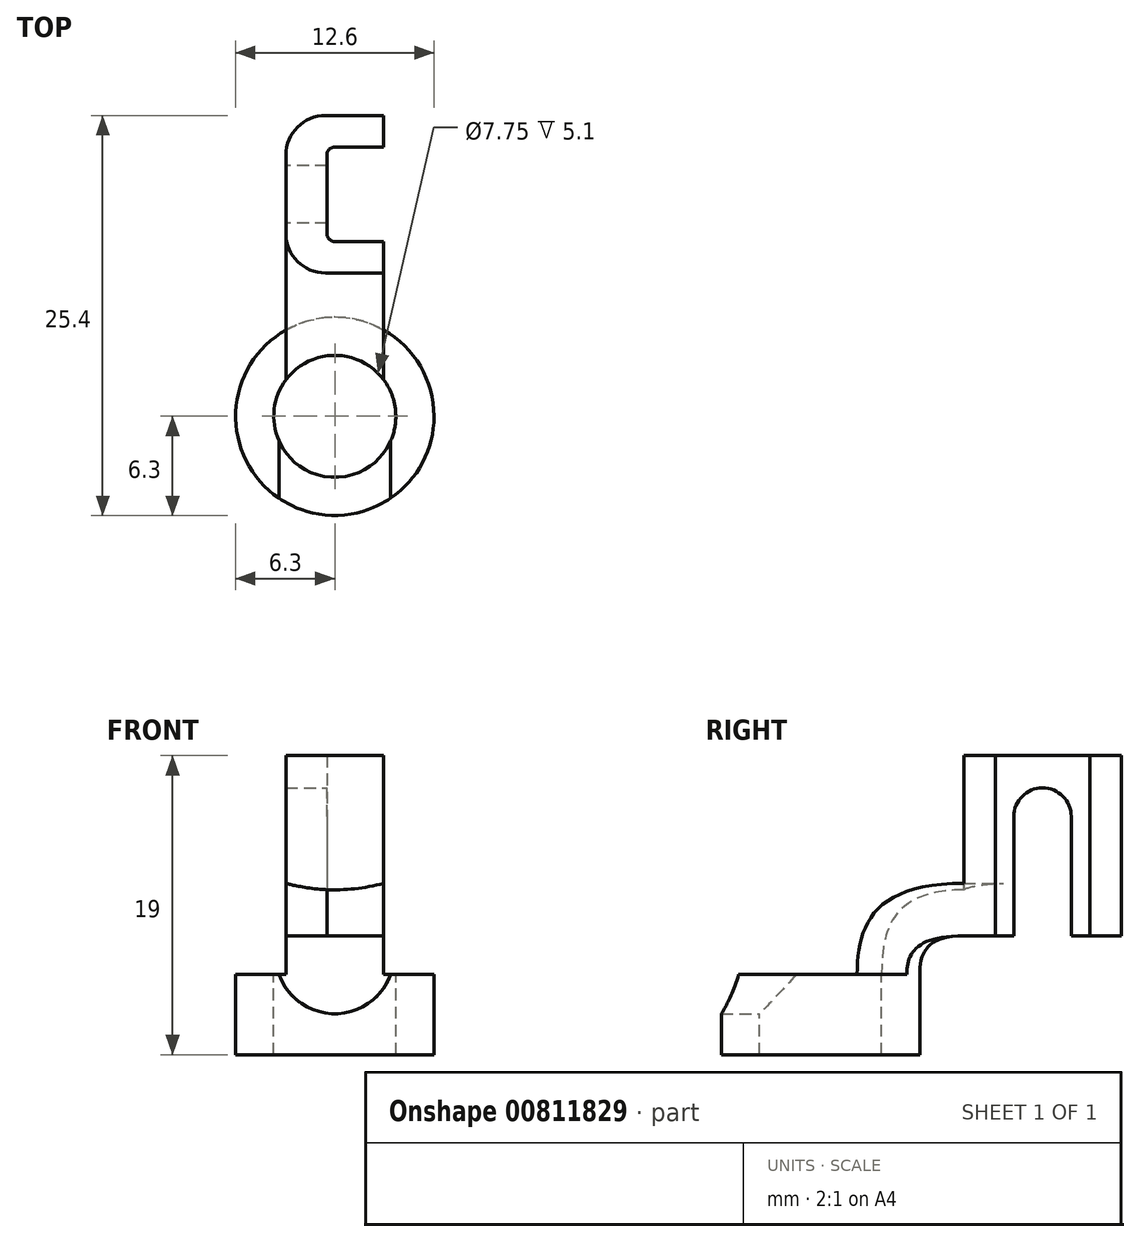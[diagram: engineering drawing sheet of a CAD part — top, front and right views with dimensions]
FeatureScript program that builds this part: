
annotation { "Feature Type Name" : "Feature", "Feature Type Description" : "" }
export const myFeature = defineFeature(function(context is Context, id is Id, definition is map)
    precondition{}
    {
        {
            var Q0;
            Q0=qCreatedBy(makeId("Top.planeOp"),FACE);
            var sketch = newSketch(context, id + "F0", { "sketchPlane" : qUnion([Q0])});
            skCircle(sketch, "E0", {"center": v(0, 0) * mm, "radius": 3.88 * mm});
            skCircle(sketch, "E1", {"center": v(0, 0) * mm, "radius": 6.3 * mm});
            skSolve(sketch);
        }
        {
            var Q0;
            Q0=qSketchRegion(id+"F0",true);
            extrude(context, id + "F1", {"entities" : qUnion([Q0]), "oppositeDirection" : true, "depth" : 5.1 * mm, "offsetDistance" : 25 * mm});
        }
        {
            var Q0;
            Q0=makeQuery(id+"F1.opExtrude","CAP_FACE",FACE,{"disambiguationData":[OSD([sQuery(id+"F0.wireOp",EDGE,"E0"),sQuery(id+"F0.wireOp",EDGE,"E1")])],"isStart":true});
            cPlane(context, id + "F2", {"entities" : qUnion([Q0]), "cplaneType" : CPlaneType.OFFSET, "offset" : (7.55 - 5.1) * mm, "width" : 150 * mm, "height" : 150 * mm});
        }
        {
            var Q0;
            Q0=qCreatedBy(id+"F2.planeOp",FACE);
            var sketch = newSketch(context, id + "F3", { "sketchPlane" : qUnion([Q0])});
            skLineSegment(sketch, "E2.bottom", {"start": v(-3.1, 9.1) * mm, "end": v(3.1, 9.1) * mm});
            skLineSegment(sketch, "E2.top", {"start": v(-3.1, 19.1) * mm, "end": v(3.1, 19.1) * mm});
            skLineSegment(sketch, "E2.left", {"start": v(-3.1, 9.1) * mm, "end": v(-3.1, 19.1) * mm});
            skLineSegment(sketch, "E2.right", {"start": v(3.1, 9.1) * mm, "end": v(3.1, 11.1) * mm});
            skLineSegment(sketch, "E3", {"start": v(-3.1, 14.1) * mm, "end": v(3.1, 14.1) * mm, "construction": true});
            skLineSegment(sketch, "E4", {"start": v(3.1, 17.1) * mm, "end": v(-0.5, 17.1) * mm});
            skLineSegment(sketch, "E5", {"start": v(-0.5, 17.1) * mm, "end": v(-0.5, 14.1) * mm});
            skLineSegment(sketch, "E6.MirrorCS", {"start": v(3.1, 11.1) * mm, "end": v(-0.5, 11.1) * mm});
            skLineSegment(sketch, "E7.MirrorCS", {"start": v(-0.5, 11.1) * mm, "end": v(-0.5, 14.1) * mm});
            skLineSegment(sketch, "E8.trimOffspring", {"start": v(3.1, 17.1) * mm, "end": v(3.1, 19.1) * mm});
            skSolve(sketch);
        }
        {
            var Q0;
            Q0=qSketchRegion(id+"F3",true);
            extrude(context, id + "F4", {"entities" : qUnion([Q0]), "depth" : 11.45 * mm, "offsetDistance" : 25 * mm});
        }
        {
            var Q0;
            Q0=makeQuery(id+"F4.opExtrude","SWEPT_FACE",FACE,{"disambiguationData":[OSD([sQuery(id+"F3.wireOp",EDGE,"E5"),sQuery(id+"F3.wireOp",EDGE,"E7.MirrorCS")])]});
            var sketch = newSketch(context, id + "F5", { "sketchPlane" : qUnion([Q0])});
            skLineSegment(sketch, "E9", {"start": v(14.1, 13.9) * mm, "end": v(14.1, 2.45) * mm, "construction": true});
            skArc(sketch, "E10", {"start": v(15.92, 10.03) * mm, "mid": v(14.1, 11.85) * mm, "end": v(12.27, 10.03) * mm});
            skLineSegment(sketch, "E11", {"start": v(12.27, 10.03) * mm, "end": v(12.27, 0.02) * mm});
            skLineSegment(sketch, "E12", {"start": v(15.92, 10.03) * mm, "end": v(15.92, 0.02) * mm});
            skArc(sketch, "E13.MirrorCS", {"start": v(15.92, 0.02) * mm, "mid": v(14.1, -1.8) * mm, "end": v(12.27, 0.02) * mm});
            skSolve(sketch);
        }
        {
            var Q0;
            Q0=qSketchRegion(id+"F5",true);
            extrude(context, id + "F6", {"entities" : qUnion([Q0]), "operationType" : NewBodyOperationType.REMOVE, "endBound" : BoundingType.UP_TO_NEXT, "oppositeDirection" : true, "depth" : 25 * mm, "offsetDistance" : 25 * mm});
        }
        {
            var Q0;
            Q0=makeQuery(id+"F4.opExtrude","SWEPT_FACE",FACE,{"disambiguationData":[OSD([sQuery(id+"F3.wireOp",EDGE,"E2.bottom")])]});
            var sketch = newSketch(context, id + "F7", { "sketchPlane" : qUnion([Q0])});
            skLineSegment(sketch, "E14.bottom", {"start": v(3.1, 5.78) * mm, "end": v(-3.1, 5.78) * mm});
            skLineSegment(sketch, "E14.left", {"start": v(3.1, -6.22) * mm, "end": v(3.1, 5.78) * mm});
            skLineSegment(sketch, "E14.right", {"start": v(-3.1, -6.22) * mm, "end": v(-3.1, 5.78) * mm});
            skPoint(sketch, "E15.centerSnap0", {"position": v(0, -6.22) * mm});
            skLineSegment(sketch, "E16", {"start": v(-3.1, -6.22) * mm, "end": v(3.1, -6.22) * mm});
            skSolve(sketch);
        }
        {
            var Q0;
            Q0=makeQuery(id+"F1.opExtrude","CAP_FACE",FACE,{"disambiguationData":[OSD([sQuery(id+"F0.wireOp",EDGE,"E0"),sQuery(id+"F0.wireOp",EDGE,"E1")])],"isStart":true});
            var sketch = newSketch(context, id + "F8", { "sketchPlane" : qUnion([Q0])});
            skCircle(sketch, "E17.0", {"center": v(0, 0) * mm, "radius": 3.88 * mm});
            skSolve(sketch);
        }
        {
            var Q0;
            {var subQ0=sQuery(id+"F7.wireOp",EDGE,"E14.bottom");Q0=makeQuery(id+"F7.imprint","IMPRINT",FACE,{"disambiguationData":[TD([[makeQuery(id+"F7.imprint","IMPRINT",EDGE,{"derivedFrom":subQ0}),-1.0]])]});}
            var sketch = newSketch(context, id + "F9", { "sketchPlane" : qUnion([Q0])});
            skLineSegment(sketch, "E18.bottom", {"start": v(3.1, 2.45) * mm, "end": v(-3.1, 2.45) * mm});
            skLineSegment(sketch, "E18.top", {"start": v(3.1, 5.78) * mm, "end": v(-3.1, 5.78) * mm, "construction": true});
            skLineSegment(sketch, "E18.left", {"start": v(3.1, 2.45) * mm, "end": v(3.1, 5.78) * mm});
            skLineSegment(sketch, "E18.right", {"start": v(-3.1, 2.45) * mm, "end": v(-3.1, 5.78) * mm});
            skArc(sketch, "E19", {"start": v(-3.1, 5.78) * mm, "mid": v(0, 5.37) * mm, "end": v(3.1, 5.78) * mm});
            skSolve(sketch);
        }
        {
            var Q0;
            Q0=makeQuery(id+"F8.imprint","IMPRINT",FACE,{"disambiguationData":[TD([[makeQuery(id+"F8.imprint","IMPRINT",EDGE,{"derivedFrom":sQuery(id+"F8.wireOp",EDGE,"E17.0")}),-1.0]])]});
            var sketch = newSketch(context, id + "F10", { "sketchPlane" : qUnion([Q0])});
            skArc(sketch, "E20.0", {"start": v(3.1, 5.48) * mm, "mid": v(0, 6.3) * mm, "end": v(-3.1, 5.48) * mm});
            skArc(sketch, "E21.0", {"start": v(3.1, 2.33) * mm, "mid": v(0, 3.88) * mm, "end": v(-3.1, 2.33) * mm});
            skLineSegment(sketch, "E22", {"start": v(-3.1, 5.48) * mm, "end": v(-3.1, 2.33) * mm});
            skLineSegment(sketch, "E23", {"start": v(0, 0) * mm, "end": v(0, 6.3) * mm, "construction": true});
            skLineSegment(sketch, "E24.MirrorCS", {"start": v(3.1, 5.48) * mm, "end": v(3.1, 2.33) * mm});
            skSolve(sketch);
        }
        {
            var Q0;
            Q0=qCreatedBy(makeId("Right.planeOp"),FACE);
            var sketch = newSketch(context, id + "F11", { "sketchPlane" : qUnion([Q0])});
            skLineSegment(sketch, "E25", {"start": v(3.88, 0) * mm, "end": v(3.88, 1) * mm, "construction": true});
            skEllipticalArc(sketch, "E26", {});
            skLineSegment(sketch, "E27", {"start": v(9.1, 5.37) * mm, "end": v(9.1, -5.37) * mm, "construction": true});
            const initialGuessF11  = {"E26": [0.0091, 0, -1, 0, 0.005225, 0.010422670097954136, 4.71238898038469, 6.283185307179586]};
            skSetInitialGuess(sketch, initialGuessF11);
            skSolve(sketch);
        }
        {
            var Q2;
            Q2=makeQuery(id+"F10.imprint","IMPRINT",FACE,{"disambiguationData":[TD([[makeQuery(id+"F10.imprint","IMPRINT",EDGE,{"derivedFrom":sQuery(id+"F10.wireOp",EDGE,"E20.0")}),1.0]])]});
            var Q3;
            Q3=makeQuery(id+"F9.imprint","IMPRINT",FACE,{"disambiguationData":[TD([[makeQuery(id+"F9.imprint","IMPRINT",EDGE,{"derivedFrom":sQuery(id+"F9.wireOp",EDGE,"E18.bottom")}),-1.0]])]});
            var Q4;
            Q4=sQuery(id+"F11.wireOp",EDGE,"E26");
            var Q5;
            Q5=sQuery(id+"F10.wireOp",VERTEX,"E20.0.end");
            var Q6;
            Q6=sQuery(id+"F9.wireOp",VERTEX,"E18.bottom.end");
            loft(context, id + "F12", {"operationType" : NewBodyOperationType.ADD, "startCondition" : LoftEndDerivativeType.NORMAL_TO_PROFILE, "startMagnitude" : 1.5, "endCondition" : LoftEndDerivativeType.NORMAL_TO_PROFILE, "endMagnitude" : 2.5, "sheetProfilesArray" : [{ "sheetProfileEntities" : qUnion([Q2]) }, { "sheetProfileEntities" : qUnion([Q3]) }], "guidesArray" : [{ "guideEntities" : qUnion([Q4]), "guideDerivativeType" : LoftGuideDerivativeType.DEFAULT, "guideDerivativeMagnitude" : 1 }], "connections" : [{ "connectionEntities" : qUnion([Q5, Q6]), "connectionEdgeQueries" : qUnion([]), "connectionEdgeParameters" : [] }]});
        }
        {
            var Q0;
            Q0=qCreatedBy(makeId("Right.planeOp"),FACE);
            var sketch = newSketch(context, id + "F13", { "sketchPlane" : qUnion([Q0])});
            skLineSegment(sketch, "E28", {"start": v(6.3, -0.55) * mm, "end": v(6.3, -5.1) * mm});
            skLineSegment(sketch, "E29", {"start": v(12.3, 2.45) * mm, "end": v(9.3, 2.45) * mm});
            skLineSegment(sketch, "E30", {"start": v(12.3, 2.45) * mm, "end": v(12.3, -5.1) * mm});
            skLineSegment(sketch, "E31", {"start": v(12.3, -5.1) * mm, "end": v(6.3, -5.1) * mm});
            skPoint(sketch, "E32.visualSharp", {"position": v(6.3, 2.45) * mm});
            skArc(sketch, "E32.filletArc", {"start": v(9.3, 2.45) * mm, "mid": v(7.18, 1.57) * mm, "end": v(6.3, -0.55) * mm});
            skSolve(sketch);
        }
        {
            var Q0;
            Q0=makeQuery(id+"F4.opExtrude","SWEPT_EDGE",EDGE,{"disambiguationData":[OSD([sQuery(id+"F3.wireOp",EDGE,"E6.MirrorCS"),sQuery(id+"F3.wireOp",EDGE,"E7.MirrorCS")])]});
            var Q1;
            Q1=makeQuery(id+"F4.opExtrude","SWEPT_EDGE",EDGE,{"disambiguationData":[OSD([sQuery(id+"F3.wireOp",EDGE,"E4"),sQuery(id+"F3.wireOp",EDGE,"E5")])]});
            fillet(context, id + "F14", {"entities" : qUnion([Q0, Q1]), "radius" : 0.5 * mm, "tangentPropagation" : true, "allowEdgeOverflow" : false});
        }
        {
            var Q0;
            Q0=makeQuery(id+"F4.opExtrude","SWEPT_EDGE",EDGE,{"disambiguationData":[OSD([sQuery(id+"F3.wireOp",EDGE,"E2.bottom"),sQuery(id+"F3.wireOp",EDGE,"E2.left")])]});
            var Q1;
            Q1=makeQuery(id+"F4.opExtrude","SWEPT_EDGE",EDGE,{"disambiguationData":[OSD([sQuery(id+"F3.wireOp",EDGE,"E2.top"),sQuery(id+"F3.wireOp",EDGE,"E2.left")])]});
            fillet(context, id + "F15", {"entities" : qUnion([Q0, Q1]), "radius" : 2.5 * mm, "tangentPropagation" : true, "allowEdgeOverflow" : false});
        }
        {
            var Q0;
            Q0=qCreatedBy(makeId("Front.planeOp"),FACE);
            var sketch = newSketch(context, id + "F16", { "sketchPlane" : qUnion([Q0])});
            skArc(sketch, "E33", {"start": v(-3.55, 0) * mm, "mid": v(0, -2.5) * mm, "end": v(3.55, 0) * mm});
            skLineSegment(sketch, "E34", {"start": v(-3.55, 0) * mm, "end": v(-3.55, -5.1) * mm, "construction": true});
            skLineSegment(sketch, "E35", {"start": v(3.55, 0) * mm, "end": v(3.55, -5.1) * mm, "construction": true});
            skLineSegment(sketch, "E36", {"start": v(0, 0) * mm, "end": v(0, 1.27) * mm, "construction": true});
            skLineSegment(sketch, "E37", {"start": v(-3.55, 0) * mm, "end": v(3.55, 0) * mm});
            skSolve(sketch);
        }
        {
            var Q0;
            Q0=qSketchRegion(id+"F16",true);
            extrude(context, id + "F17", {"entities" : qUnion([Q0]), "operationType" : NewBodyOperationType.REMOVE, "endBound" : BoundingType.THROUGH_ALL, "depth" : 25 * mm, "offsetDistance" : 25 * mm});
        }
    });
